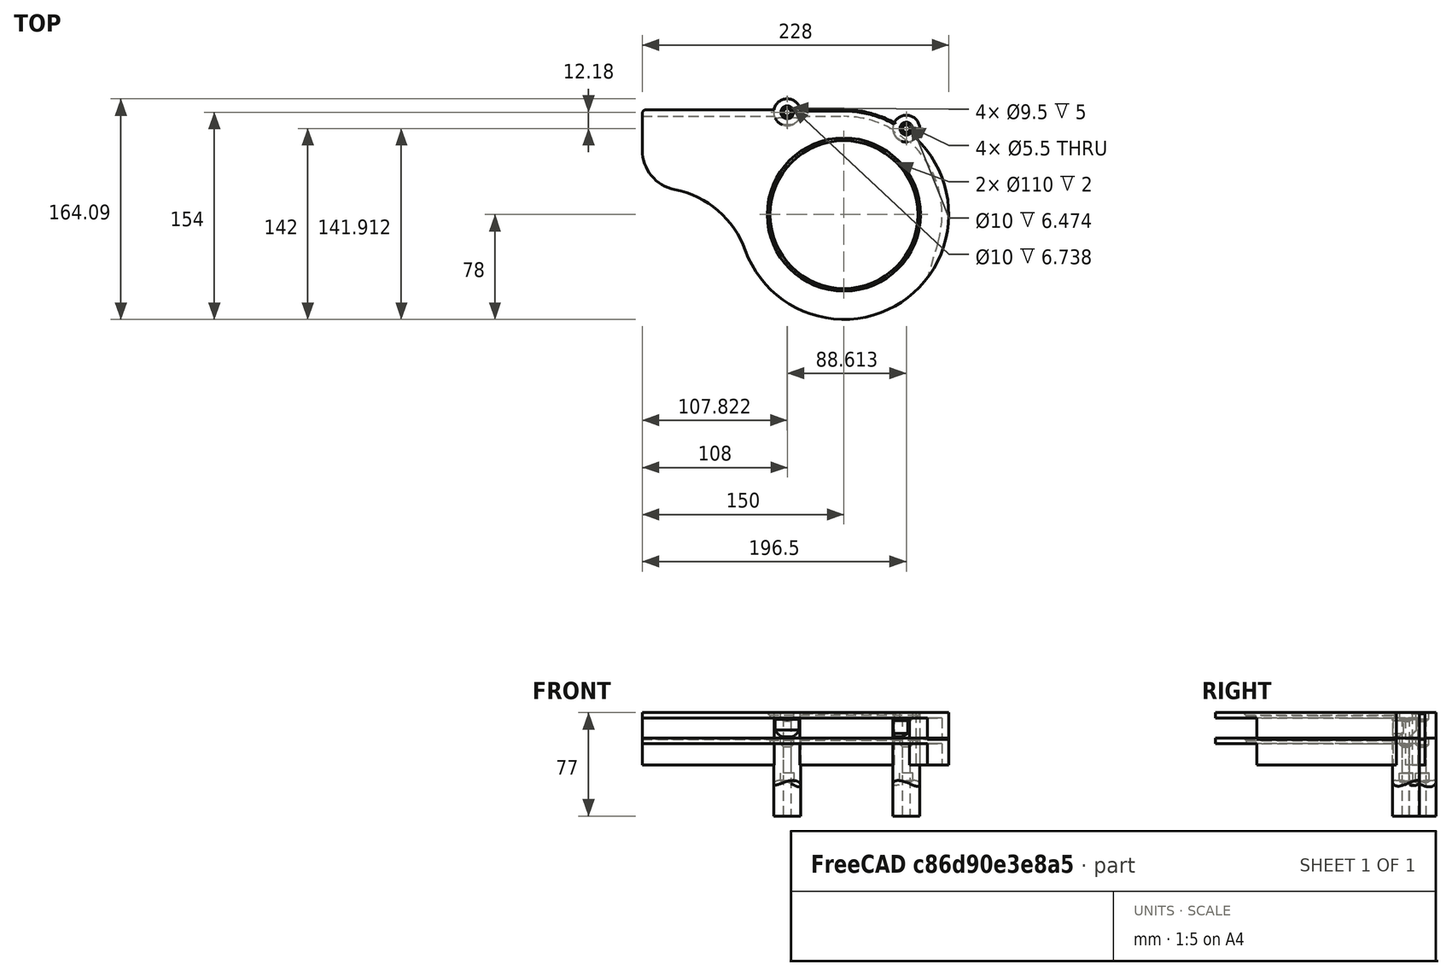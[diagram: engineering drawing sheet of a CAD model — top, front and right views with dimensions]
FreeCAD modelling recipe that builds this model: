
FCSTD DOCUMENT  (FreeCAD 0.19R)
Label: R4
License: All rights reserved
LicenseURL: http://en.wikipedia.org/wiki/All_rights_reserved
objects: Part::Cylinder×6, Sketcher::SketchObject×5, Part::Cut×4, PartDesign::Pocket×3, PartDesign::Chamfer×3, PartDesign::Pad×2, Part::MultiFuse×2, Part::Chamfer×2, PartDesign::Fillet×1, PartDesign::Body×1, Mesh::Feature×1
note: 38 computed .brp shape members not serialized (recipe doc carries the construction recipe); baked Part::Feature solids carry a one-line shape summary decoded from their .brp

FEATURE [Sketcher::SketchObject] Sketch
  FullyConstrained = true
  MapMode = 5
  Support = -> [XY_Plane]
  sketch-geometry (10):
    g0: LineSegment StartX=0 StartY=0 StartZ=0 EndX=121.094 EndY=169.768 EndZ=0
    g1: LineSegment StartX=-81.2548 StartY=143.617 StartZ=0 EndX=0 EndY=0 EndZ=0
    g2: Circle CenterX=0 CenterY=0 CenterZ=0 NormalX=0 NormalY=0 NormalZ=1 AngleXU=0 Radius=73
    g3: LineSegment StartX=-228.06 StartY=73 StartZ=0 EndX=0 EndY=73 EndZ=0
    g4: LineSegment StartX=2.39e-14 StartY=78 StartZ=0 EndX=-150 EndY=78 EndZ=0
    g5: ArcOfCircle CenterX=0 CenterY=0 CenterZ=0 NormalX=0 NormalY=0 NormalZ=1 AngleXU=0 Radius=78 StartAngle=3.48916 EndAngle=7.85398
    g6: LineSegment StartX=-150 StartY=78 StartZ=0 EndX=-150 EndY=48 EndZ=0
    g7: ArcOfCircle CenterX=-120 CenterY=48 CenterZ=0 NormalX=0 NormalY=0 NormalZ=1 AngleXU=0 Radius=30 StartAngle=3.14159 EndAngle=4.51567
    g8: ArcOfCircle CenterX=-139.648 CenterY=-50.5912 CenterZ=0 NormalX=0 NormalY=0 NormalZ=1 AngleXU=0 Radius=70.53 StartAngle=0.347568 EndAngle=1.37408
    g9: Circle CenterX=0 CenterY=0 CenterZ=0 NormalX=0 NormalY=0 NormalZ=1 AngleXU=0 Radius=55
  constraints (28):
    c: Coincident(g0,g-1)
    c: Coincident(g1,g-1)
    c: Angle(g1) = -1.05592
    c: Angle(g0,g1) = 1.13446
    c: Coincident(g2,g-1)
    c: Radius(g2) = 73
    c: Tangent(g3,g2)
    c: Angle(g3) = 0
    c: PointOnObject(g4,g-2)
    c: Coincident(g5,g-1)
    c: Coincident(g5,g4)
    c: Radius(g5) = 78
    c: Coincident(g6,g4)
    c: Vertical(g6)
    c: Tangent(g5,g8) = 1.5708
    c: Tangent(g8,g7) = 1.5708
    c: Tangent(g7,g6) = -1.5708
    c: Distance(g4) = 150
    c: Radius(g7) = 30
    c: Radius(g8) = 70.53
    c: Horizontal(g4)
    c: Distance(g6) = 30
    c: Distance(g0) = 208.53
    c: Distance(g1) = 165.01
    c: Distance(g3) = 228.06
    c: PointOnObject(g3,g-2)
    c: Coincident(g9,g5)
    c: Radius(g9) = 55
FEATURE [PartDesign::Pad] Pad
  Direction = (1,1,1)
  Length = 20
  Length2 = 100
  Profile = -> Sketch
  Type = 0
FEATURE [Sketcher::SketchObject] Sketch001
  FullyConstrained = true
  MapMode = 5
  Placement = pos=(0,0,0) rot=(1,0,0;3.14159rad)
  Support = -> [Pad]
  sketch-geometry (4):
    g0: LineSegment StartX=-300 StartY=-73 StartZ=0 EndX=0 EndY=-73 EndZ=0
    g1: ArcOfCircle CenterX=0 CenterY=0 CenterZ=0 NormalX=0 NormalY=0 NormalZ=1 AngleXU=0 Radius=73 StartAngle=4.71239 EndAngle=6.57087
    g2: LineSegment StartX=70 StartY=20.7123 StartZ=0 EndX=34.9593 EndY=139.137 EndZ=0
    g3: LineSegment StartX=34.9593 StartY=139.137 StartZ=0 EndX=-300 EndY=-73 EndZ=0
  constraints (11):
    c: PointOnObject(g0,g-2)
    c: Horizontal(g0)
    c: Coincident(g1,g-1)
    c: Coincident(g1,g0)
    c: DistanceX(g1) = 70
    c: Radius(g1) = 73
    c: Tangent(g1,g2) = -1.5708
    c: Coincident(g2,g3)
    c: Coincident(g3,g0)
    c: Distance(g2) = 123.5
    c: Distance(g0) = 300
FEATURE [PartDesign::Pocket] Pocket
  BaseFeature = -> Pad
  Length = 16
  Length2 = 100
  Profile = -> Sketch001
  Type = 0
FEATURE [Sketcher::SketchObject] Sketch002
  FullyConstrained = true
  MapMode = 5
  Placement = pos=(0,0,20) rot=(0,0,1;0rad)
  Support = -> [Pocket]
  sketch-geometry (4):
    g0: LineSegment StartX=-72.7214 StartY=131.193 StartZ=0 EndX=0 EndY=0 EndZ=0
    g1: LineSegment StartX=0 StartY=0 StartZ=0 EndX=88.1678 EndY=121.353 EndZ=0
    g2: Circle CenterX=-42.1784 CenterY=76.0919 CenterZ=0 NormalX=0 NormalY=0 NormalZ=1 AngleXU=0 Radius=10
    g3: Circle CenterX=46.435 CenterY=63.9123 CenterZ=0 NormalX=0 NormalY=0 NormalZ=1 AngleXU=0 Radius=10
  constraints (12):
    c: Coincident(g0,g-1)
    c: Angle(g0) = -1.06465
    c: Coincident(g1,g-1)
    c: Angle(g1,g0) = 1.13446
    c: Distance(g1) = 150
    c: Distance(g0) = 150
    c: Diameter(g3) = 20
    c: Equal(g3,g2)
    c: PointOnObject(g2,g0)
    c: PointOnObject(g3,g1)
    c: Distance(g-1,g3) = 79
    c: Distance(g-1,g2) = 87
FEATURE [PartDesign::Pad] Pad001
  BaseFeature = -> Pocket
  Direction = (1,1,1)
  Length = 58
  Length2 = 100
  Profile = -> Sketch002
  Reversed = true
  Type = 0
FEATURE [Sketcher::SketchObject] Sketch003
  ExternalGeometry = -> [Pad001]
  FullyConstrained = true
  MapMode = 5
  Placement = pos=(0,0,20) rot=(0,0,1;0rad)
  Support = -> [Pad001]
  sketch-geometry (2):
    g0: Circle CenterX=-42.1784 CenterY=76.0919 CenterZ=0 NormalX=0 NormalY=0 NormalZ=1 AngleXU=0 Radius=2.75
    g1: Circle CenterX=46.435 CenterY=63.9123 CenterZ=0 NormalX=0 NormalY=0 NormalZ=1 AngleXU=0 Radius=2.75
  constraints (4):
    c: Diameter(g0) = 5.5
    c: Equal(g0,g1)
    c: Coincident(g0,g-3)
    c: Coincident(g1,g-4)
FEATURE [PartDesign::Pocket] Pocket001
  BaseFeature = -> Pad001
  Length = 5
  Length2 = 100
  Profile = -> Sketch003
  Type = 1
FEATURE [Sketcher::SketchObject] Sketch004
  ExternalGeometry = -> [Pocket001]
  FullyConstrained = true
  MapMode = 5
  Placement = pos=(0,0,20) rot=(0,0,1;0rad)
  Support = -> [Pocket001]
  sketch-geometry (2):
    g0: Circle CenterX=46.435 CenterY=63.9123 CenterZ=0 NormalX=0 NormalY=0 NormalZ=1 AngleXU=0 Radius=4.75
    g1: Circle CenterX=-42.1784 CenterY=76.0919 CenterZ=0 NormalX=0 NormalY=0 NormalZ=1 AngleXU=0 Radius=4.75
  constraints (4):
    c: Diameter(g1) = 9.5
    c: Coincident(g1,g-4)
    c: Coincident(g0,g-5)
    c: Diameter(g0) = 9.5
FEATURE [PartDesign::Pocket] Pocket002
  BaseFeature = -> Pocket001
  Length = 5
  Length2 = 100
  Profile = -> Sketch004
  Type = 0
FEATURE [Part::Cylinder] Cylinder
  Angle = 360
  AttacherType = Attacher::AttachEngine3D
  Height = 100
  Placement = pos=(0,0,-45) rot=(-0.810679,0.585491,0;1.5708rad)
  Radius = 14.5
FEATURE [Part::Cylinder] Cylinder001
  Angle = 360
  AttacherType = Attacher::AttachEngine3D
  Height = 100
  Placement = pos=(0,0,-45) rot=(-0.8704,-0.492345,0;1.5708rad)
  Radius = 14.5
FEATURE [Part::Cylinder] Cylinder002
  Angle = 360
  AttacherType = Attacher::AttachEngine3D
  Height = 10
  Placement = pos=(-42,76,-35) rot=(0,0,1;0rad)
  Radius = 5
FEATURE [Part::Cylinder] Cylinder003
  Angle = 360
  AttacherType = Attacher::AttachEngine3D
  Height = 10
  Placement = pos=(46.5,64,-35) rot=(0,0,1;0rad)
  Radius = 5
FEATURE [Part::MultiFuse] Fusion
  Shapes = -> [Cylinder,Cylinder001]
FEATURE [Part::MultiFuse] Fusion001
  Shapes = -> [Cylinder003,Cylinder002]
FEATURE [PartDesign::Chamfer] Chamfer
  Angle = 45
  Base = -> Pocket002 [Edge82,Edge78]
  BaseFeature = -> Pocket002
  ChamferType = 0
  FlipDirection = false
  Size = 1.6
  Size2 = 1
  SupportTransform = false
FEATURE [PartDesign::Chamfer] Chamfer001
  Angle = 45
  Base = -> Chamfer [Edge66]
  BaseFeature = -> Chamfer
  ChamferType = 0
  FlipDirection = false
  Size = 2
  Size2 = 1
  SupportTransform = false
FEATURE [PartDesign::Chamfer] Chamfer002
  Angle = 45
  Base = -> Chamfer001 [Edge11]
  BaseFeature = -> Chamfer001
  ChamferType = 0
  FlipDirection = false
  Size = 1
  Size2 = 1
  SupportTransform = false
FEATURE [PartDesign::Fillet] Fillet
  Base = -> Chamfer002 [Edge38]
  BaseFeature = -> Chamfer002
  Radius = 3
  SupportTransform = false
FEATURE [PartDesign::Body] Body
  Group = -> [Sketch,Pad,Sketch001,Pocket,Sketch002,Pad001,Sketch003,Pocket001,Sketch004,Pocket002,Chamfer,Chamfer001,Chamfer002,Fillet]
  Origin = -> Origin
  Tip = -> Fillet
FEATURE [Part::Cut] Cut
  Base = -> Fillet
  Tool = -> Fusion
FEATURE [Part::Cut] Cut001
  Base = -> Cut
  Placement = pos=(0,0,19) rot=(0,0,1;0rad)
  Tool = -> Fusion001
FEATURE [Part::Cylinder] Cylinder004
  Angle = 360
  AttacherType = Attacher::AttachEngine3D
  Height = 12
  Placement = pos=(0,0,21) rot=(0,0,1;0rad)
  Radius = 72
FEATURE [Part::Cut] Cut002
  Base = -> Cut001
  Tool = -> Cylinder004
FEATURE [Part::Cylinder] Cylinder005
  Angle = 360
  AttacherType = Attacher::AttachEngine3D
  Height = 13
  Placement = pos=(-42,-14,21) rot=(0,0,1;0rad)
  Radius = 86
FEATURE [Part::Cut] Cut003
  Base = -> Cut002
  Tool = -> Cylinder005
FEATURE [Part::Chamfer] Chamfer003
  Base = -> Cut003
  Edges = 1 edges r=5.1: [Edge110]
FEATURE [Part::Chamfer] Chamfer004
  Base = -> Chamfer003
  Edges = 1 edges r=2.6: [Edge125]
FEATURE [Mesh::Feature] Mesh  label="Chamfer004 (Meshed)"
